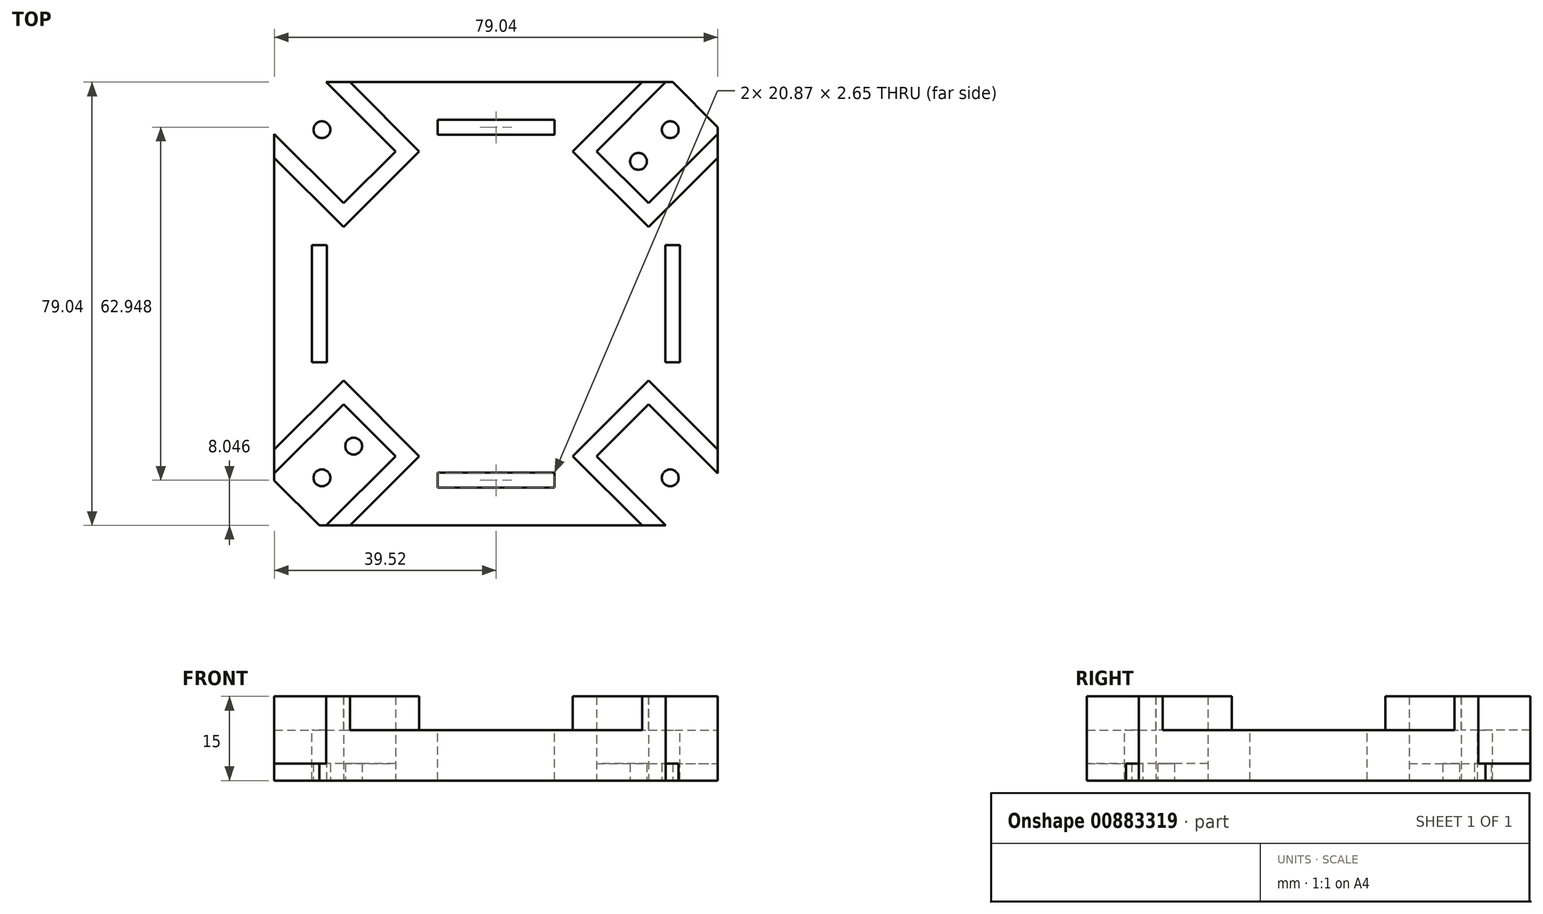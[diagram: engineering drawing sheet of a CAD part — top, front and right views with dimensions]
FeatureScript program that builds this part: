
annotation { "Feature Type Name" : "Feature", "Feature Type Description" : "" }
export const myFeature = defineFeature(function(context is Context, id is Id, definition is map)
    precondition{}
    {
        {
            var Q0;
            Q0=qCreatedBy(makeId("Top.planeOp"),FACE);
            var sketch = newSketch(context, id + "F0", { "sketchPlane" : qUnion([Q0])});
            skPoint(sketch, "E0.7.0", {"position": v(30.02, 20.75) * mm});
            skPoint(sketch, "E0.7.1", {"position": v(35.67, 26.41) * mm});
            skPoint(sketch, "E0.7.2", {"position": v(38.64, 29.38) * mm});
            skPoint(sketch, "E0.7.3", {"position": v(20.75, 30.02) * mm});
            skPoint(sketch, "E0.7.4", {"position": v(29.38, 38.64) * mm});
            skLineSegment(sketch, "E0.7.5", {"start": v(27.19, 17.93) * mm, "end": v(39.52, 30.26) * mm});
            skPoint(sketch, "E0.7.6", {"position": v(28.28, 28.28) * mm});
            skLineSegment(sketch, "E0.7.7", {"start": v(27.19, 17.93) * mm, "end": v(17.93, 27.19) * mm});
            skLineSegment(sketch, "E0.7.8", {"start": v(17.93, 27.19) * mm, "end": v(27.26, 36.52) * mm});
            skPoint(sketch, "E0.7.9", {"position": v(26.41, 35.67) * mm});
            skCircle(sketch, "E0.7.10", {"center": v(31.04, 31.04) * mm, "radius": 1.5 * mm});
            skCircle(sketch, "E0.7.11", {"center": v(25.39, 25.39) * mm, "radius": 1.5 * mm});
            skPoint(sketch, "E0.center", {"position": v(0, 0) * mm});
            skLineSegment(sketch, "E1.0", {"start": v(0, 39.52) * mm, "end": v(27.26, 39.52) * mm});
            skLineSegment(sketch, "E2.0", {"start": v(39.52, 27.26) * mm, "end": v(39.52, 0) * mm});
            skLineSegment(sketch, "E3.0", {"start": v(31.5, 39.52) * mm, "end": v(27.26, 39.52) * mm});
            skLineSegment(sketch, "E4.0", {"start": v(39.52, 31.5) * mm, "end": v(39.52, 27.26) * mm});
            skLineSegment(sketch, "E5", {"start": v(31.5, 39.52) * mm, "end": v(39.52, 31.5) * mm});
            skLineSegment(sketch, "E6.MirrorCS", {"start": v(17.93, 27.19) * mm, "end": v(30.26, 39.52) * mm});
            skPoint(sketch, "E7.MirrorP", {"position": v(27.26, 36.52) * mm});
            skLineSegment(sketch, "E8.MirrorCS", {"start": v(27.19, 17.93) * mm, "end": v(36.52, 27.26) * mm});
            skLineSegment(sketch, "E9.MirrorCS", {"start": v(-31.5, 39.52) * mm, "end": v(-27.26, 39.52) * mm});
            skLineSegment(sketch, "E10.MirrorCS", {"start": v(-39.52, 31.5) * mm, "end": v(-39.52, 27.26) * mm});
            skCircle(sketch, "E11.MirrorC", {"center": v(-31.04, 31.04) * mm, "radius": 1.5 * mm});
            skLineSegment(sketch, "E12.MirrorCS", {"start": v(-17.93, 27.19) * mm, "end": v(-27.26, 36.52) * mm});
            skCircle(sketch, "E13.MirrorC", {"center": v(-25.39, 25.39) * mm, "radius": 1.5 * mm});
            skLineSegment(sketch, "E14.MirrorCS", {"start": v(-27.19, 17.93) * mm, "end": v(-39.52, 30.26) * mm});
            skLineSegment(sketch, "E15.MirrorCS", {"start": v(-17.93, 27.19) * mm, "end": v(-30.26, 39.52) * mm});
            skLineSegment(sketch, "E16.MirrorCS", {"start": v(-27.19, 17.93) * mm, "end": v(-36.52, 27.26) * mm});
            skLineSegment(sketch, "E17.MirrorCS", {"start": v(0, 39.52) * mm, "end": v(-27.26, 39.52) * mm});
            skPoint(sketch, "E18.MirrorP", {"position": v(-38.64, 29.38) * mm});
            skPoint(sketch, "E19.MirrorP", {"position": v(-28.28, 28.28) * mm});
            skPoint(sketch, "E20.MirrorP", {"position": v(-35.67, 26.41) * mm});
            skLineSegment(sketch, "E21.MirrorCS", {"start": v(-31.5, 39.52) * mm, "end": v(-39.52, 31.5) * mm});
            skPoint(sketch, "E22.MirrorP", {"position": v(-26.41, 35.67) * mm});
            skPoint(sketch, "E23.MirrorP", {"position": v(-29.38, 38.64) * mm});
            skPoint(sketch, "E24.MirrorP", {"position": v(-20.75, 30.02) * mm});
            skPoint(sketch, "E25.MirrorP", {"position": v(-30.02, 20.75) * mm});
            skLineSegment(sketch, "E26.MirrorCS", {"start": v(-27.19, 17.93) * mm, "end": v(-17.93, 27.19) * mm});
            skPoint(sketch, "E27.MirrorP", {"position": v(-27.26, 36.52) * mm});
            skLineSegment(sketch, "E28.MirrorCS", {"start": v(-39.52, 27.26) * mm, "end": v(-39.52, 0) * mm});
            skLineSegment(sketch, "E29.MirrorCS", {"start": v(-39.52, -31.5) * mm, "end": v(-39.52, -27.26) * mm});
            skLineSegment(sketch, "E30.MirrorCS", {"start": v(39.52, -31.5) * mm, "end": v(39.52, -27.26) * mm});
            skLineSegment(sketch, "E31.MirrorCS", {"start": v(-31.5, -39.52) * mm, "end": v(-27.26, -39.52) * mm});
            skLineSegment(sketch, "E32.MirrorCS", {"start": v(31.5, -39.52) * mm, "end": v(27.26, -39.52) * mm});
            skCircle(sketch, "E33.MirrorC", {"center": v(31.04, -31.04) * mm, "radius": 1.5 * mm});
            skCircle(sketch, "E34.MirrorC", {"center": v(-31.04, -31.04) * mm, "radius": 1.5 * mm});
            skCircle(sketch, "E35.MirrorC", {"center": v(25.39, -25.39) * mm, "radius": 1.5 * mm});
            skLineSegment(sketch, "E36.MirrorCS", {"start": v(17.93, -27.19) * mm, "end": v(27.26, -36.52) * mm});
            skLineSegment(sketch, "E37.MirrorCS", {"start": v(-17.93, -27.19) * mm, "end": v(-27.26, -36.52) * mm});
            skCircle(sketch, "E38.MirrorC", {"center": v(-25.39, -25.39) * mm, "radius": 1.5 * mm});
            skLineSegment(sketch, "E39.MirrorCS", {"start": v(27.19, -17.93) * mm, "end": v(39.52, -30.26) * mm});
            skLineSegment(sketch, "E40.MirrorCS", {"start": v(-17.93, -27.19) * mm, "end": v(-30.26, -39.52) * mm});
            skLineSegment(sketch, "E41.MirrorCS", {"start": v(-27.19, -17.93) * mm, "end": v(-36.52, -27.26) * mm});
            skLineSegment(sketch, "E42.MirrorCS", {"start": v(17.93, -27.19) * mm, "end": v(30.26, -39.52) * mm});
            skLineSegment(sketch, "E43.MirrorCS", {"start": v(27.19, -17.93) * mm, "end": v(36.52, -27.26) * mm});
            skLineSegment(sketch, "E44.MirrorCS", {"start": v(-27.19, -17.93) * mm, "end": v(-39.52, -30.26) * mm});
            skPoint(sketch, "E45.MirrorP", {"position": v(-35.67, -26.41) * mm});
            skPoint(sketch, "E46.MirrorP", {"position": v(-29.38, -38.64) * mm});
            skLineSegment(sketch, "E47.MirrorCS", {"start": v(-31.5, -39.52) * mm, "end": v(-39.52, -31.5) * mm});
            skPoint(sketch, "E48.MirrorP", {"position": v(38.64, -29.38) * mm});
            skPoint(sketch, "E49.MirrorP", {"position": v(20.75, -30.02) * mm});
            skPoint(sketch, "E50.MirrorP", {"position": v(26.41, -35.67) * mm});
            skPoint(sketch, "E51.MirrorP", {"position": v(35.67, -26.41) * mm});
            skLineSegment(sketch, "E52.MirrorCS", {"start": v(0, -39.52) * mm, "end": v(27.26, -39.52) * mm});
            skLineSegment(sketch, "E53.MirrorCS", {"start": v(31.5, -39.52) * mm, "end": v(39.52, -31.5) * mm});
            skPoint(sketch, "E54.MirrorP", {"position": v(-28.28, -28.28) * mm});
            skPoint(sketch, "E55.MirrorP", {"position": v(-26.41, -35.67) * mm});
            skLineSegment(sketch, "E56.MirrorCS", {"start": v(0, -39.52) * mm, "end": v(-27.26, -39.52) * mm});
            skPoint(sketch, "E57.MirrorP", {"position": v(-20.75, -30.02) * mm});
            skPoint(sketch, "E58.MirrorP", {"position": v(-38.64, -29.38) * mm});
            skPoint(sketch, "E59.MirrorP", {"position": v(29.38, -38.64) * mm});
            skPoint(sketch, "E60.MirrorP", {"position": v(28.28, -28.28) * mm});
            skPoint(sketch, "E61.MirrorP", {"position": v(27.26, -36.52) * mm});
            skPoint(sketch, "E62.MirrorP", {"position": v(-27.26, -36.52) * mm});
            skPoint(sketch, "E63.MirrorP", {"position": v(-30.02, -20.75) * mm});
            skPoint(sketch, "E64.MirrorP", {"position": v(30.02, -20.75) * mm});
            skLineSegment(sketch, "E65.MirrorCS", {"start": v(-27.19, -17.93) * mm, "end": v(-17.93, -27.19) * mm});
            skLineSegment(sketch, "E66.MirrorCS", {"start": v(27.19, -17.93) * mm, "end": v(17.93, -27.19) * mm});
            skLineSegment(sketch, "E67.MirrorCS", {"start": v(39.52, -27.26) * mm, "end": v(39.52, 0) * mm});
            skLineSegment(sketch, "E68.MirrorCS", {"start": v(-39.52, -27.26) * mm, "end": v(-39.52, 0) * mm});
            skSolve(sketch);
        }
        {
            var Q0;
            {var subQ18=sQuery(id+"F0.wireOp",EDGE,"E0.7.7");Q0=makeQuery(id+"F0.imprint","IMPRINT",FACE,{"disambiguationData":[TD([[makeQuery(id+"F0.imprint","IMPRINT",EDGE,{"derivedFrom":subQ18}),1.0]])]});}
            extrude(context, id + "F1", {"entities" : qUnion([Q0]), "depth" : 12 * mm, "offsetDistance" : 25.4 * mm});
        }
        {
            var Q0;
            Q0=makeQuery(id+"F0.imprint","IMPRINT",FACE,{"disambiguationData":[TD([[makeQuery(id+"F0.imprint","IMPRINT",EDGE,{"derivedFrom":sQuery(id+"F0.wireOp",EDGE,"E34.MirrorC")}),-1.0]])]});
            var Q1;
            Q1=makeQuery(id+"F0.imprint","IMPRINT",FACE,{"disambiguationData":[TD([[makeQuery(id+"F0.imprint","IMPRINT",EDGE,{"derivedFrom":sQuery(id+"F0.wireOp",EDGE,"E11.MirrorC")}),1.0]])]});
            var Q2;
            {var subQ0=sQuery(id+"F0.wireOp",EDGE,"E0.7.7");Q2=makeQuery(id+"F0.imprint","IMPRINT",FACE,{"disambiguationData":[TD([[makeQuery(id+"F0.imprint","IMPRINT",EDGE,{"derivedFrom":subQ0}),-1.0]])]});}
            var Q3;
            Q3=makeQuery(id+"F0.imprint","IMPRINT",FACE,{"disambiguationData":[TD([[makeQuery(id+"F0.imprint","IMPRINT",EDGE,{"derivedFrom":sQuery(id+"F0.wireOp",EDGE,"E33.MirrorC")}),1.0]])]});
            var Q4;
            Q4=makeQuery(id+"F1.opExtrude","CAP_FACE",FACE,{"disambiguationData":[OSD([sQuery(id+"F0.wireOp",EDGE,"E0.7.5"),sQuery(id+"F0.wireOp",EDGE,"E0.7.7"),sQuery(id+"F0.wireOp",EDGE,"E0.7.8"),sQuery(id+"F0.wireOp",EDGE,"E1.0"),sQuery(id+"F0.wireOp",EDGE,"E2.0"),sQuery(id+"F0.wireOp",EDGE,"E3.0"),sQuery(id+"F0.wireOp",EDGE,"E4.0"),sQuery(id+"F0.wireOp",EDGE,"E6.MirrorCS"),sQuery(id+"F0.wireOp",EDGE,"E9.MirrorCS"),sQuery(id+"F0.wireOp",EDGE,"E10.MirrorCS"),sQuery(id+"F0.wireOp",EDGE,"E12.MirrorCS"),sQuery(id+"F0.wireOp",EDGE,"E14.MirrorCS"),sQuery(id+"F0.wireOp",EDGE,"E15.MirrorCS"),sQuery(id+"F0.wireOp",EDGE,"E17.MirrorCS"),sQuery(id+"F0.wireOp",EDGE,"E26.MirrorCS"),sQuery(id+"F0.wireOp",EDGE,"E28.MirrorCS"),sQuery(id+"F0.wireOp",EDGE,"E29.MirrorCS"),sQuery(id+"F0.wireOp",EDGE,"E30.MirrorCS"),sQuery(id+"F0.wireOp",EDGE,"E31.MirrorCS"),sQuery(id+"F0.wireOp",EDGE,"E32.MirrorCS"),sQuery(id+"F0.wireOp",EDGE,"E36.MirrorCS"),sQuery(id+"F0.wireOp",EDGE,"E37.MirrorCS"),sQuery(id+"F0.wireOp",EDGE,"E39.MirrorCS"),sQuery(id+"F0.wireOp",EDGE,"E40.MirrorCS"),sQuery(id+"F0.wireOp",EDGE,"E41.MirrorCS"),sQuery(id+"F0.wireOp",EDGE,"E42.MirrorCS"),sQuery(id+"F0.wireOp",EDGE,"E44.MirrorCS"),sQuery(id+"F0.wireOp",EDGE,"E52.MirrorCS"),sQuery(id+"F0.wireOp",EDGE,"E56.MirrorCS"),sQuery(id+"F0.wireOp",EDGE,"E65.MirrorCS"),sQuery(id+"F0.wireOp",EDGE,"E66.MirrorCS"),sQuery(id+"F0.wireOp",EDGE,"E67.MirrorCS"),sQuery(id+"F0.wireOp",EDGE,"E68.MirrorCS")])],"isStart":false});
            extrude(context, id + "F2", {"entities" : qUnion([Q0, Q1, Q2, Q3, Q4]), "operationType" : NewBodyOperationType.ADD, "depth" : 3 * mm, "offsetDistance" : 25.4 * mm});
        }
        {
            var Q0;
            Q0=makeQuery(id+"F2.opExtrude","CAP_FACE",FACE,{"disambiguationData":[OSD([sQuery(id+"F0.wireOp",EDGE,"E0.7.5"),sQuery(id+"F0.wireOp",EDGE,"E0.7.7"),sQuery(id+"F0.wireOp",EDGE,"E0.7.8"),sQuery(id+"F0.wireOp",EDGE,"E1.0"),sQuery(id+"F0.wireOp",EDGE,"E2.0"),sQuery(id+"F0.wireOp",EDGE,"E3.0"),sQuery(id+"F0.wireOp",EDGE,"E4.0"),sQuery(id+"F0.wireOp",EDGE,"E6.MirrorCS"),sQuery(id+"F0.wireOp",EDGE,"E9.MirrorCS"),sQuery(id+"F0.wireOp",EDGE,"E10.MirrorCS"),sQuery(id+"F0.wireOp",EDGE,"E12.MirrorCS"),sQuery(id+"F0.wireOp",EDGE,"E14.MirrorCS"),sQuery(id+"F0.wireOp",EDGE,"E15.MirrorCS"),sQuery(id+"F0.wireOp",EDGE,"E17.MirrorCS"),sQuery(id+"F0.wireOp",EDGE,"E26.MirrorCS"),sQuery(id+"F0.wireOp",EDGE,"E28.MirrorCS"),sQuery(id+"F0.wireOp",EDGE,"E29.MirrorCS"),sQuery(id+"F0.wireOp",EDGE,"E30.MirrorCS"),sQuery(id+"F0.wireOp",EDGE,"E31.MirrorCS"),sQuery(id+"F0.wireOp",EDGE,"E32.MirrorCS"),sQuery(id+"F0.wireOp",EDGE,"E36.MirrorCS"),sQuery(id+"F0.wireOp",EDGE,"E37.MirrorCS"),sQuery(id+"F0.wireOp",EDGE,"E39.MirrorCS"),sQuery(id+"F0.wireOp",EDGE,"E40.MirrorCS"),sQuery(id+"F0.wireOp",EDGE,"E41.MirrorCS"),sQuery(id+"F0.wireOp",EDGE,"E42.MirrorCS"),sQuery(id+"F0.wireOp",EDGE,"E44.MirrorCS"),sQuery(id+"F0.wireOp",EDGE,"E52.MirrorCS"),sQuery(id+"F0.wireOp",EDGE,"E56.MirrorCS"),sQuery(id+"F0.wireOp",EDGE,"E65.MirrorCS"),sQuery(id+"F0.wireOp",EDGE,"E66.MirrorCS"),sQuery(id+"F0.wireOp",EDGE,"E67.MirrorCS"),sQuery(id+"F0.wireOp",EDGE,"E68.MirrorCS")])],"isStart":false});
            var sketch = newSketch(context, id + "F3", { "sketchPlane" : qUnion([Q0])});
            skLineSegment(sketch, "E69", {"start": v(-13.68, 27.19) * mm, "end": v(13.68, 27.19) * mm});
            skLineSegment(sketch, "E70", {"start": v(27.19, 13.68) * mm, "end": v(27.19, 0) * mm});
            skLineSegment(sketch, "E71", {"start": v(-27.19, 0) * mm, "end": v(-27.19, 13.68) * mm});
            skLineSegment(sketch, "E72.0", {"start": v(13.68, 27.19) * mm, "end": v(26.02, 39.52) * mm});
            skLineSegment(sketch, "E73.0", {"start": v(-26.02, 39.52) * mm, "end": v(-13.68, 27.19) * mm});
            skLineSegment(sketch, "E74.0", {"start": v(-39.52, 26.02) * mm, "end": v(-27.19, 13.68) * mm});
            skLineSegment(sketch, "E75.0", {"start": v(27.19, 13.68) * mm, "end": v(39.52, 26.02) * mm});
            skLineSegment(sketch, "E76", {"start": v(-27.19, 13.68) * mm, "end": v(-13.68, 27.19) * mm});
            skLineSegment(sketch, "E77", {"start": v(13.68, 27.19) * mm, "end": v(27.19, 13.68) * mm});
            skLineSegment(sketch, "E78", {"start": v(-26.02, 39.52) * mm, "end": v(26.02, 39.52) * mm});
            skLineSegment(sketch, "E79", {"start": v(39.52, 26.02) * mm, "end": v(39.52, 0) * mm});
            skLineSegment(sketch, "E80", {"start": v(-39.52, 26.02) * mm, "end": v(-39.52, 0) * mm});
            skLineSegment(sketch, "E81.MirrorCS", {"start": v(13.68, -27.19) * mm, "end": v(27.19, -13.68) * mm});
            skLineSegment(sketch, "E82.MirrorCS", {"start": v(-27.19, 0) * mm, "end": v(-27.19, -13.68) * mm});
            skLineSegment(sketch, "E83.MirrorCS", {"start": v(27.19, -13.68) * mm, "end": v(39.52, -26.02) * mm});
            skLineSegment(sketch, "E84.MirrorCS", {"start": v(-39.52, -26.02) * mm, "end": v(-27.19, -13.68) * mm});
            skLineSegment(sketch, "E85.MirrorCS", {"start": v(-13.68, -27.19) * mm, "end": v(13.68, -27.19) * mm});
            skLineSegment(sketch, "E86.MirrorCS", {"start": v(39.52, -26.02) * mm, "end": v(39.52, 0) * mm});
            skLineSegment(sketch, "E87.MirrorCS", {"start": v(-27.19, -13.68) * mm, "end": v(-13.68, -27.19) * mm});
            skLineSegment(sketch, "E88.MirrorCS", {"start": v(27.19, -13.68) * mm, "end": v(27.19, 0) * mm});
            skLineSegment(sketch, "E89.MirrorCS", {"start": v(-39.52, -26.02) * mm, "end": v(-39.52, 0) * mm});
            skLineSegment(sketch, "E90.MirrorCS", {"start": v(13.68, -27.19) * mm, "end": v(26.02, -39.52) * mm});
            skLineSegment(sketch, "E91.MirrorCS", {"start": v(-26.02, -39.52) * mm, "end": v(-13.68, -27.19) * mm});
            skLineSegment(sketch, "E92.MirrorCS", {"start": v(-26.02, -39.52) * mm, "end": v(26.02, -39.52) * mm});
            skSolve(sketch);
        }
        {
            var Q0;
            Q0 = qSketchRegion(id + "F3", true);
            extrude(context, id + "F4", {"entities" : qUnion([Q0]), "operationType" : NewBodyOperationType.REMOVE, "oppositeDirection" : true, "depth" : 6 * mm, "offsetDistance" : 25.4 * mm});
        }
        {
            var Q0;
            Q0=makeQuery(id+"F4.boolean.opBoolean","COPY",FACE,{"derivedFrom":makeQuery(id+"F4.opExtrude","CAP_FACE",FACE,{"disambiguationData":[OSD([sQuery(id+"F3.wireOp",EDGE,"E72.0"),sQuery(id+"F3.wireOp",EDGE,"E73.0"),sQuery(id+"F3.wireOp",EDGE,"E74.0"),sQuery(id+"F3.wireOp",EDGE,"E75.0"),sQuery(id+"F3.wireOp",EDGE,"E76"),sQuery(id+"F3.wireOp",EDGE,"E77"),sQuery(id+"F3.wireOp",EDGE,"E78"),sQuery(id+"F3.wireOp",EDGE,"E79"),sQuery(id+"F3.wireOp",EDGE,"E80"),sQuery(id+"F3.wireOp",EDGE,"E81.MirrorCS"),sQuery(id+"F3.wireOp",EDGE,"E83.MirrorCS"),sQuery(id+"F3.wireOp",EDGE,"E84.MirrorCS"),sQuery(id+"F3.wireOp",EDGE,"E86.MirrorCS"),sQuery(id+"F3.wireOp",EDGE,"E87.MirrorCS"),sQuery(id+"F3.wireOp",EDGE,"E89.MirrorCS"),sQuery(id+"F3.wireOp",EDGE,"E90.MirrorCS"),sQuery(id+"F3.wireOp",EDGE,"E91.MirrorCS"),sQuery(id+"F3.wireOp",EDGE,"E92.MirrorCS")])],"isStart":false})});
            var sketch = newSketch(context, id + "F5", { "sketchPlane" : qUnion([Q0])});
            skLineSegment(sketch, "E93.bottom", {"start": v(10.44, 30.15) * mm, "end": v(-10.44, 30.15) * mm});
            skLineSegment(sketch, "E93.top", {"start": v(10.44, 32.8) * mm, "end": v(-10.44, 32.8) * mm});
            skLineSegment(sketch, "E93.left", {"start": v(10.44, 30.15) * mm, "end": v(10.44, 32.8) * mm});
            skLineSegment(sketch, "E93.right", {"start": v(-10.44, 30.15) * mm, "end": v(-10.44, 32.8) * mm});
            skPoint(sketch, "E93.middle", {"position": v(0, 31.47) * mm});
            skLineSegment(sketch, "E94.1.0", {"start": v(-32.8, 10.44) * mm, "end": v(-32.8, -10.44) * mm});
            skLineSegment(sketch, "E94.1.1", {"start": v(-30.15, -10.44) * mm, "end": v(-32.8, -10.44) * mm});
            skLineSegment(sketch, "E94.1.2", {"start": v(-30.15, 10.44) * mm, "end": v(-32.8, 10.44) * mm});
            skLineSegment(sketch, "E94.1.3", {"start": v(-30.15, 10.44) * mm, "end": v(-30.15, -10.44) * mm});
            skPoint(sketch, "E94.1.4", {"position": v(-31.47, 0) * mm});
            skLineSegment(sketch, "E94.2.0", {"start": v(-10.44, -32.8) * mm, "end": v(10.44, -32.8) * mm});
            skLineSegment(sketch, "E94.2.1", {"start": v(10.44, -30.15) * mm, "end": v(10.44, -32.8) * mm});
            skLineSegment(sketch, "E94.2.2", {"start": v(-10.44, -30.15) * mm, "end": v(-10.44, -32.8) * mm});
            skLineSegment(sketch, "E94.2.3", {"start": v(-10.44, -30.15) * mm, "end": v(10.44, -30.15) * mm});
            skPoint(sketch, "E94.2.4", {"position": v(0, -31.47) * mm});
            skLineSegment(sketch, "E94.3.0", {"start": v(32.8, -10.44) * mm, "end": v(32.8, 10.44) * mm});
            skLineSegment(sketch, "E94.3.1", {"start": v(30.15, 10.44) * mm, "end": v(32.8, 10.44) * mm});
            skLineSegment(sketch, "E94.3.2", {"start": v(30.15, -10.44) * mm, "end": v(32.8, -10.44) * mm});
            skLineSegment(sketch, "E94.3.3", {"start": v(30.15, -10.44) * mm, "end": v(30.15, 10.44) * mm});
            skPoint(sketch, "E94.3.4", {"position": v(31.47, 0) * mm});
            skPoint(sketch, "E94.center", {"position": v(0, 0) * mm});
            skSolve(sketch);
        }
        {
            var Q0;
            Q0 = qSketchRegion(id + "F5", true);
            extrude(context, id + "F6", {"entities" : qUnion([Q0]), "operationType" : NewBodyOperationType.REMOVE, "endBound" : BoundingType.THROUGH_ALL, "oppositeDirection" : true, "depth" : 25.4 * mm, "offsetDistance" : 25.4 * mm});
        }
    });
